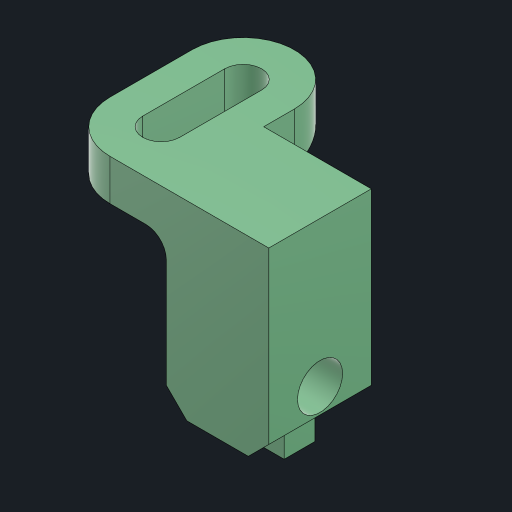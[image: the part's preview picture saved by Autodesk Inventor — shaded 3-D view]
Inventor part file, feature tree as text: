
AUTODESK INVENTOR PART (.ipt)
format: ipt  version: 2023 (Build 270158000, 158)  size: 197,120 bytes
history: native  units: mm
features: sketch x3, extrude x3, other x2, hole x1, fillet x1, chamfer x1
ambient origin geometry x8: Origin, YZ Plane, XZ Plane, XY Plane, X Axis, Y Axis, Z Axis, Center Point
bodies: Body1 (feature_tree)
feature tree (11):
  other  "ソリッド1"
  sketch  "スケッチ1"
  extrude  "押し出し1"  Depth=1.8mm
  extrude  "押し出し4"  Depth=4.0mm
  hole  "穴3"  [1 undecoded]
  fillet  "フィレット3"  Radius=2.0mm
  other  "作業平面2"
  chamfer  "面取り1"  Distance=7.3mm
  extrude  "押し出し5"  Depth=5.0mm
  sketch  "スケッチ6"
  sketch  "スケッチ7"
note: 1 required parameter value undecoded (feature->parameter linkage not recoverable at this tier; creation-order binding heuristic only, values carry confidence <= 0.55)
